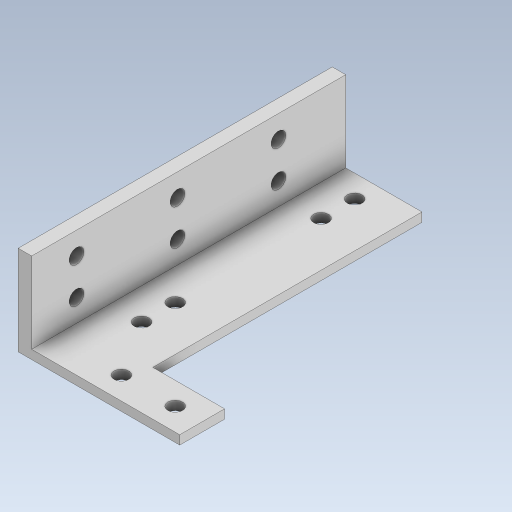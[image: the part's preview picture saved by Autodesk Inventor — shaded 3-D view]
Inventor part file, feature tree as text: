
AUTODESK INVENTOR PART (.ipt)
format: ipt  version: 2023.5 (Build 275446000, 446)  size: 160,256 bytes
history: native  units: mm
features: extrude x3, sketch x2
ambient origin geometry x8: Origin, YZ Plane, XZ Plane, XY Plane, X Axis, Y Axis, Z Axis, Center Point
bodies: Solid1 (feature_tree)
feature tree (5):
  sketch  "Sketch1"  dims[d10=2.0mm d11=0.0mm d12=20.0mm d13=0.0mm]
  extrude  "Extrusion1"  Depth=20.0mm TaperAngle=0.0deg
  extrude  "Extrusion2"  Depth=20.0mm
  extrude  "Extrusion4"  Depth=20.0mm
  sketch  "Sketch3"  dims[d22=3.3mm d23=20.0mm d24=3.3mm d25=40.0mm d26=5.0mm d27=3.3mm d28=5.0mm d29=10.0mm d30=3.3mm d31=22.5mm d32=3.3mm d33=8.0mm d34=3.3mm d35=20.0mm d36=0.0mm]
